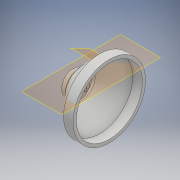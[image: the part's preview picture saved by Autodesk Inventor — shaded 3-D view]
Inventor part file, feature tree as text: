
AUTODESK INVENTOR PART (.ipt)
format: ipt  version: 2018 (Build 220112000, 112)  size: 2,698,240 bytes
history: native  units: mm
features: sketch x75, extrude x67, fillet x27, revolve x3, plane x3, mirror x1
ambient origin geometry x8: Origin, YZ Plane, XZ Plane, XY Plane, X Axis, Y Axis, Z Axis, Center Point
bodies: Solid1 (feature_tree)
feature tree (176):
  extrude  "Extrusion1"  TaperAngle=0.0deg  [1 undecoded]
  extrude  "Extrusion2"  Depth=10.0mm TaperAngle=0.0deg
  extrude  "Extrusion3"  Depth=10.0mm
  extrude  "Extrusion4"  TaperAngle=0.0deg  [1 undecoded]
  extrude  "Extrusion5"  Depth=10.0mm TaperAngle=0.0deg
  sketch  "Sketch6"  dims[d19=10.0mm d20=0.0mm d21=40.0mm]
  extrude  "Extrusion6"  Depth=10.0mm
  extrude  "Extrusion7"  Depth=11.0mm TaperAngle=0.0deg
  extrude  "Extrusion8"  Depth=32.0mm TaperAngle=0.0deg
  extrude  "Extrusion9"  Depth=32.0mm TaperAngle=0.0deg
  extrude  "Extrusion10"  Depth=10.0mm TaperAngle=0.0deg
  extrude  "Extrusion11"  Depth=10.0mm TaperAngle=0.0deg
  extrude  "Extrusion12"  TaperAngle=0.0deg  [1 undecoded]
  extrude  "Extrusion14"  Depth=48.3mm
  extrude  "Extrusion15"  TaperAngle=0.0deg  [1 undecoded]
  extrude  "Extrusion16"  Depth=10.0mm TaperAngle=0.0deg
  extrude  "Extrusion17"  Depth=11.63mm TaperAngle=0.0deg
  sketch  "Sketch21"  dims[d83=0.0mm d84=0.0mm d85=0.0mm d86=0.0mm]
  extrude  "Extrusion19"  Depth=11.63mm TaperAngle=0.0deg
  extrude  "Extrusion20"  TaperAngle=0.0deg  [1 undecoded]
  extrude  "Extrusion21"  Depth=10.0mm TaperAngle=0.0deg
  extrude  "Extrusion22"  TaperAngle=0.0deg  [1 undecoded]
  extrude  "Extrusion23"  Depth=2.86mm TaperAngle=0.0deg
  extrude  "Extrusion24"  Depth=2.01mm
  extrude  "Extrusion25"  Depth=10.0mm TaperAngle=0.0deg
  sketch  "Sketch33"  dims[d115=7.8mm d116=0.0mm d117=0.0mm d118=0.0mm]
  extrude  "Extrusion26"  Depth=10.0mm TaperAngle=0.0deg
  extrude  "Extrusion27"  TaperAngle=0.0deg  [1 undecoded]
  extrude  "Extrusion28"  Depth=22.0mm TaperAngle=0.0deg
  extrude  "Extrusion29"  Depth=17.0mm TaperAngle=0.0deg
  extrude  "Extrusion30"  Depth=2.0mm
  extrude  "Extrusion31"  Depth=6.95mm TaperAngle=0.0deg
  extrude  "Extrusion32"  Depth=18.0mm TaperAngle=0.0deg
  extrude  "Extrusion33"  Depth=1.02mm
  sketch  "Sketch42"  dims[d151=2.0mm d152=2.0mm]
  extrude  "Extrusion34"  Depth=7.72mm TaperAngle=0.0deg
  extrude  "Extrusion36"  Depth=2.0mm
  extrude  "Extrusion37"  Depth=2.0mm
  revolve  "Revolution3"  [1 undecoded]
  extrude  "Extrusion38"  Depth=2.0mm
  extrude  "Extrusion39"  Depth=10.0mm TaperAngle=0.0deg
  fillet  "Fillet1"  Radius=7.83mm
  fillet  "Fillet2"  Radius=20.0mm
  sketch  "Sketch51"  dims[d171=2.0mm d172=2.0mm]
  extrude  "Extrusion41"  Depth=6.4mm TaperAngle=0.0deg
  mirror  "Mirror1"
  extrude  "Extrusion42"  Depth=2.0mm
  sketch  "Sketch54"  dims[d181=2.0mm d182=2.0mm]
  sketch  "Sketch55"  dims[d183=2.0mm d184=2.0mm]
  sketch  "Sketch56"  dims[d185=2.0mm d186=0.0mm d187=0.0mm]
  extrude  "Extrusion44"  Depth=2.0mm
  extrude  "Extrusion45"  Depth=2.0mm
  extrude  "Extrusion46"  TaperAngle=90.0deg  [1 undecoded]
  extrude  "Extrusion47"  Depth=2.0mm
  plane  "Work Plane2"
  extrude  "Extrusion48"  Depth=2.0mm
  extrude  "Extrusion49"  TaperAngle=0.0deg  [1 undecoded]
  plane  "Work Plane5"
  extrude  "Extrusion50"  TaperAngle=0.0deg  [1 undecoded]
  extrude  "Extrusion51"  Depth=10.0mm
  fillet  "Fillet3"  Radius=10.0mm
  fillet  "Fillet4"  Radius=2.0mm
  extrude  "Extrusion52"  Depth=29.0mm
  extrude  "Extrusion53"  Depth=13.7mm
  extrude  "Extrusion54"  Depth=7.82mm TaperAngle=0.0deg
  extrude  "Extrusion55"  Depth=18.0mm TaperAngle=0.0deg
  fillet  "Fillet5"  [1 undecoded]
  extrude  "Extrusion57"  [1 undecoded]
  extrude  "Extrusion58"  [1 undecoded]
  extrude  "Extrusion59"  [1 undecoded]
  fillet  "Fillet7"  [1 undecoded]
  fillet  "Fillet8"  [1 undecoded]
  fillet  "Fillet9"  [1 undecoded]
  fillet  "Fillet10"  [1 undecoded]
  fillet  "Fillet11"  [1 undecoded]
  fillet  "Fillet12"  [1 undecoded]
  fillet  "Fillet13"  [1 undecoded]
  fillet  "Fillet14"  [1 undecoded]
  extrude  "Extrusion60"  [1 undecoded]
  extrude  "Extrusion61"  [1 undecoded]
  extrude  "Extrusion62"  [1 undecoded]
  extrude  "Extrusion63"  [1 undecoded]
  extrude  "Extrusion64"  [1 undecoded]
  extrude  "Extrusion65"  [1 undecoded]
  fillet  "Fillet15"  [1 undecoded]
  fillet  "Fillet16"  [1 undecoded]
  fillet  "Fillet17"  [1 undecoded]
  fillet  "Fillet18"  [1 undecoded]
  fillet  "Fillet19"  [1 undecoded]
  revolve  "Revolution4"  [1 undecoded]
  fillet  "Fillet20"  [1 undecoded]
  fillet  "Fillet21"  [1 undecoded]
  fillet  "Fillet22"  [1 undecoded]
  fillet  "Fillet23"  [1 undecoded]
  fillet  "Fillet24"  [1 undecoded]
  extrude  "Extrusion66"  [1 undecoded]
  revolve  "Revolution5"  [1 undecoded]
  sketch  "Sketch86"
  extrude  "Extrusion67"  [1 undecoded]
  extrude  "Extrusion68"  [1 undecoded]
  plane  "Work Plane6"
  extrude  "Extrusion69"  [1 undecoded]
  fillet  "Fillet25"  [1 undecoded]
  fillet  "Fillet26"  [1 undecoded]
  extrude  "Extrusion70"  [1 undecoded]
  fillet  "Fillet27"  [1 undecoded]
  fillet  "Fillet28"  [1 undecoded]
  extrude  "Extrusion71"  [1 undecoded]
  extrude  "Extrusion72"  [1 undecoded]
  extrude  "Extrusion73"  [1 undecoded]
  sketch  "Sketch1"  dims[d0=10.0mm d1=0.0mm d2=0.0mm d3=0.0mm]
  sketch  "Sketch2"  dims[d4=0.0mm d5=0.0mm d6=10.0mm d7=0.0mm]
  sketch  "Sketch3"  dims[d8=10.0mm d9=0.0mm d10=50.0mm]
  sketch  "Sketch4"  dims[d11=10.0mm d12=0.0mm d13=0.0mm d14=0.0mm]
  sketch  "Sketch5"  dims[d15=0.0mm d16=0.0mm d17=10.0mm d18=0.0mm]
  sketch  "Sketch7"  dims[d22=38.0mm d23=11.0mm d24=0.0mm]
  sketch  "Sketch8"  dims[d25=9.5mm d26=0.0mm d33=32.0mm d34=0.0mm]
  sketch  "Sketch9"  dims[d37=32.0mm d38=0.0mm d39=32.0mm d40=0.0mm]
  sketch  "Sketch10"  dims[d41=32.0mm d42=0.0mm d45=10.0mm d46=0.0mm]
  sketch  "Sketch11"  dims[d47=10.0mm d48=0.0mm d49=10.0mm d50=0.0mm]
  sketch  "Sketch12"  dims[d51=0.0mm d52=0.0mm d53=0.0mm d54=0.0mm]
  sketch  "Sketch13"  dims[d65=46.0mm d66=48.3mm]
  sketch  "Sketch16"  dims[d67=9.0mm d68=0.0mm d69=0.0mm d70=0.0mm]
  sketch  "Sketch18"  dims[d71=0.0mm d72=0.0mm d73=10.0mm d74=0.0mm]
  sketch  "Sketch19"  dims[d75=5.0mm d76=0.0mm d77=11.63mm d78=0.0mm]
  sketch  "Sketch20"  dims[d79=11.63mm d80=0.0mm d81=11.63mm d82=0.0mm]
  sketch  "Sketch22"  dims[d87=30.0mm d88=10.0mm d89=0.0mm]
  sketch  "Sketch23"  dims[d92=10.0mm d93=0.0mm d94=0.0mm d95=0.0mm]
  sketch  "Sketch24"  dims[d96=135.0deg d99=2.86mm d100=0.0mm]
  sketch  "Sketch25"  dims[d101=0.0mm d102=0.0mm d105=2.01mm]
  sketch  "Sketch31"  dims[d106=2.22mm d107=10.0mm d108=0.0mm]
  sketch  "Sketch32"  dims[d109=10.0mm d110=0.0mm d113=7.8mm d114=0.0mm]
  sketch  "Sketch34"  dims[d119=16.0mm d120=0.0mm d121=22.0mm d122=0.0mm]
  sketch  "Sketch35"  dims[d123=22.0mm d124=0.0mm d126=17.0mm d127=0.0mm]
  sketch  "Sketch36"  dims[d128=17.0mm d129=0.0mm d130=2.0mm]
  sketch  "Sketch37"  dims[d131=2.0mm d132=6.95mm d133=0.0mm]
  sketch  "Sketch38"  dims[d134=6.95mm d135=0.0mm d136=18.0mm d137=0.0mm]
  sketch  "Sketch39"  dims[d138=16.0mm d139=0.0mm d140=1.02mm]
  sketch  "Sketch40"  dims[d143=15.5mm d144=0.0mm d146=7.72mm d147=0.0mm]
  sketch  "Sketch41"  dims[d148=17.0mm d149=0.0mm d150=2.0mm]
  sketch  "Sketch43"  dims[d153=2.0mm d154=2.0mm]
  sketch  "Sketch45"  dims[d155=2.0mm d156=2.0mm]
  sketch  "Sketch47"  dims[d157=2.0mm d158=10.0mm d159=0.0mm d160=7.83mm d161=0.0mm d162=20.0mm d163=0.0mm]
  sketch  "Sketch48"  dims[d164=0.0mm d165=0.0mm d166=6.4mm d167=0.0mm]
  sketch  "Sketch49"  dims[d168=6.14mm d169=0.0mm d170=2.0mm]
  sketch  "Sketch52"  dims[d173=2.0mm d174=2.0mm]
  sketch  "Sketch53"  dims[d175=1.5mm d176=1.5mm d177=3.0mm d178=10.0mm d180=90.0deg]
  sketch  "Sketch57"  dims[d192=90.0deg d193=0.0mm d194=0.0mm]
  sketch  "Sketch60"  dims[d195=10.0mm d196=0.0mm d197=15.0mm d198=10.0mm d199=0.0mm d200=2.0mm]
  sketch  "Sketch61"  dims[d201=2.0mm d202=29.0mm]
  sketch  "Sketch62"  dims[d203=0.8mm d204=0.0mm d205=13.7mm]
  sketch  "Sketch63"  dims[d206=2.0mm d207=7.82mm d208=0.0mm]
  sketch  "Sketch65"  dims[d209=0.0mm d210=0.0mm d211=18.0mm d212=0.0mm]
  sketch  "Sketch66"
  sketch  "Sketch67"
  sketch  "Sketch68"
  sketch  "Sketch69"
  sketch  "Sketch70"
  sketch  "Sketch72"
  sketch  "Sketch73"
  sketch  "Sketch74"
  sketch  "Sketch75"
  sketch  "Sketch76"
  sketch  "Sketch78"
  sketch  "Sketch80"
  sketch  "Sketch81"
  sketch  "Sketch82"
  sketch  "Sketch83"
  sketch  "Sketch84"
  sketch  "Sketch85"
  sketch  "Sketch87"
  sketch  "Sketch88"
  sketch  "Sketch89"
  sketch  "Sketch91"
  sketch  "Sketch92"
  sketch  "Sketch93"
note: 53 required parameter values undecoded (feature->parameter linkage not recoverable at this tier; creation-order binding heuristic only, values carry confidence <= 0.55)